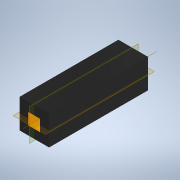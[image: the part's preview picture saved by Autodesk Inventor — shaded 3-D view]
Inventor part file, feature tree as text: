
AUTODESK INVENTOR PART (.ipt)
format: ipt  version: 2020 (Build 240168000, 168)  size: 101,376 bytes
history: native  units: in
note: dims shown in document units (in); Inventor stores cm internally (conversion verified against a paired STEP export)
features: other x2, plane x2
ambient origin geometry x8: Origin, YZ Plane, XZ Plane, XY Plane, X Axis, Y Axis, Z Axis, Center Point
bodies: Solid1 (feature_tree)
feature tree (4):
  other  "Work Axis1"
  plane  "Work Plane1"
  plane  "Work Plane2"
  other  "Part1"
